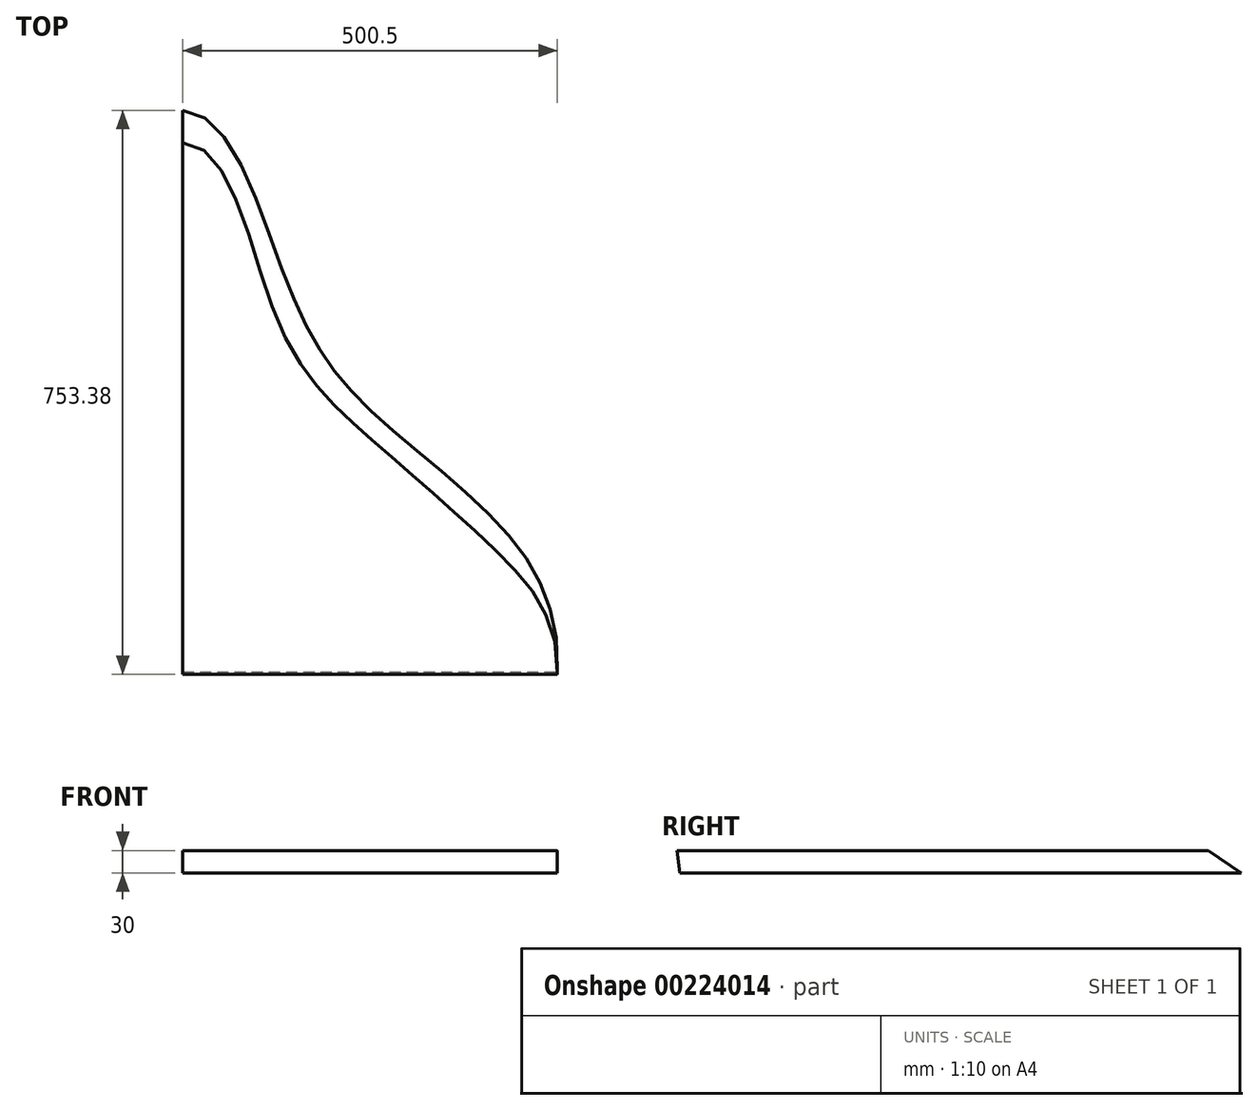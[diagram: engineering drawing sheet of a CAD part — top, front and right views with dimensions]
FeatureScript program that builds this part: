
annotation { "Feature Type Name" : "Feature", "Feature Type Description" : "" }
export const myFeature = defineFeature(function(context is Context, id is Id, definition is map)
    precondition{}
    {
        {
            var Q0;
            Q0=qCreatedBy(makeId("Top.planeOp"),FACE);
            var sketch = newSketch(context, id + "F0", { "sketchPlane" : qUnion([Q0])});
            skFitSpline(sketch, "E0", {"points": [v(0, 750) * mm, v(132.91, 536.26) * mm, v(238.12, 361.5) * mm, v(423.68, 195.8) * mm, v(500, 0) * mm], "startDerivative": vector(735.09, -10.2) * mm, "endDerivative": vector(-52.08, -1026.85) * mm});
            skLineSegment(sketch, "E1", {"start": v(0, 750) * mm, "end": v(0, 0) * mm});
            skLineSegment(sketch, "E2", {"start": v(0, 0) * mm, "end": v(500, 0) * mm});
            skSolve(sketch);
        }
        {
            var Q0;
            Q0=qCreatedBy(makeId("Top.planeOp"),FACE);
            cPlane(context, id + "F1", {"entities" : qUnion([Q0]), "cplaneType" : CPlaneType.OFFSET, "offset" : 30 * mm, "width" : 150 * mm, "height" : 150 * mm});
        }
        {
            var Q0;
            Q0=qCreatedBy(id+"F1.planeOp",FACE);
            var sketch = newSketch(context, id + "F2", { "sketchPlane" : qUnion([Q0])});
            skFitSpline(sketch, "E3", {"points": [v(-0.12, 706.62) * mm, v(125.53, 472.6) * mm, v(250.75, 311.87) * mm, v(404, 175.43) * mm, v(499.88, -3.38) * mm], "startDerivative": vector(735.09, -10.2) * mm, "endDerivative": vector(-52.08, -1026.85) * mm});
            skLineSegment(sketch, "E4", {"start": v(-0.12, 706.62) * mm, "end": v(-0.12, -3.38) * mm});
            skLineSegment(sketch, "E5", {"start": v(-0.12, -3.38) * mm, "end": v(499.88, -3.38) * mm});
            skSolve(sketch);
        }
        {
            var Q0;
            Q0=makeQuery(id+"F2.imprint","IMPRINT",FACE,{"disambiguationData":[TD([[makeQuery(id+"F2.imprint","IMPRINT",EDGE,{"derivedFrom":sQuery(id+"F2.wireOp",EDGE,"E3")}),-1.0]])]});
            var Q1;
            Q1=makeQuery(id+"F0.imprint","IMPRINT",FACE,{"disambiguationData":[TD([[makeQuery(id+"F0.imprint","IMPRINT",EDGE,{"derivedFrom":sQuery(id+"F0.wireOp",EDGE,"E0")}),-1.0]])]});
            loft(context, id + "F3", {"sheetProfilesArray" : [{ "sheetProfileEntities" : qUnion([Q0]) }, { "sheetProfileEntities" : qUnion([Q1]) }]});
        }
        {
            var Q0;
            Q0=qCreatedBy(makeId("Front.planeOp"),FACE);
            cPlane(context, id + "F4", {"entities" : qUnion([Q0]), "cplaneType" : CPlaneType.OFFSET, "offset" : 250 * mm, "width" : 150 * mm, "height" : 150 * mm});
        }
        {
            var Q0;
            Q0=qCreatedBy(id+"F4.planeOp",FACE);
            cPlane(context, id + "F5", {"entities" : qUnion([Q0]), "cplaneType" : CPlaneType.OFFSET, "offset" : 250 * mm, "width" : 150 * mm, "height" : 150 * mm});
        }
        {
            var Q0;
            Q0=qCreatedBy(id+"F5.planeOp",FACE);
            cPlane(context, id + "F6", {"entities" : qUnion([Q0]), "cplaneType" : CPlaneType.OFFSET, "offset" : 250 * mm, "width" : 150 * mm, "height" : 150 * mm});
        }
        {
            var Q0;
            Q0=qCreatedBy(id+"F6.planeOp",FACE);
            cPlane(context, id + "F7", {"entities" : qUnion([Q0]), "cplaneType" : CPlaneType.OFFSET, "offset" : 250 * mm, "width" : 150 * mm, "height" : 150 * mm});
        }
    });
